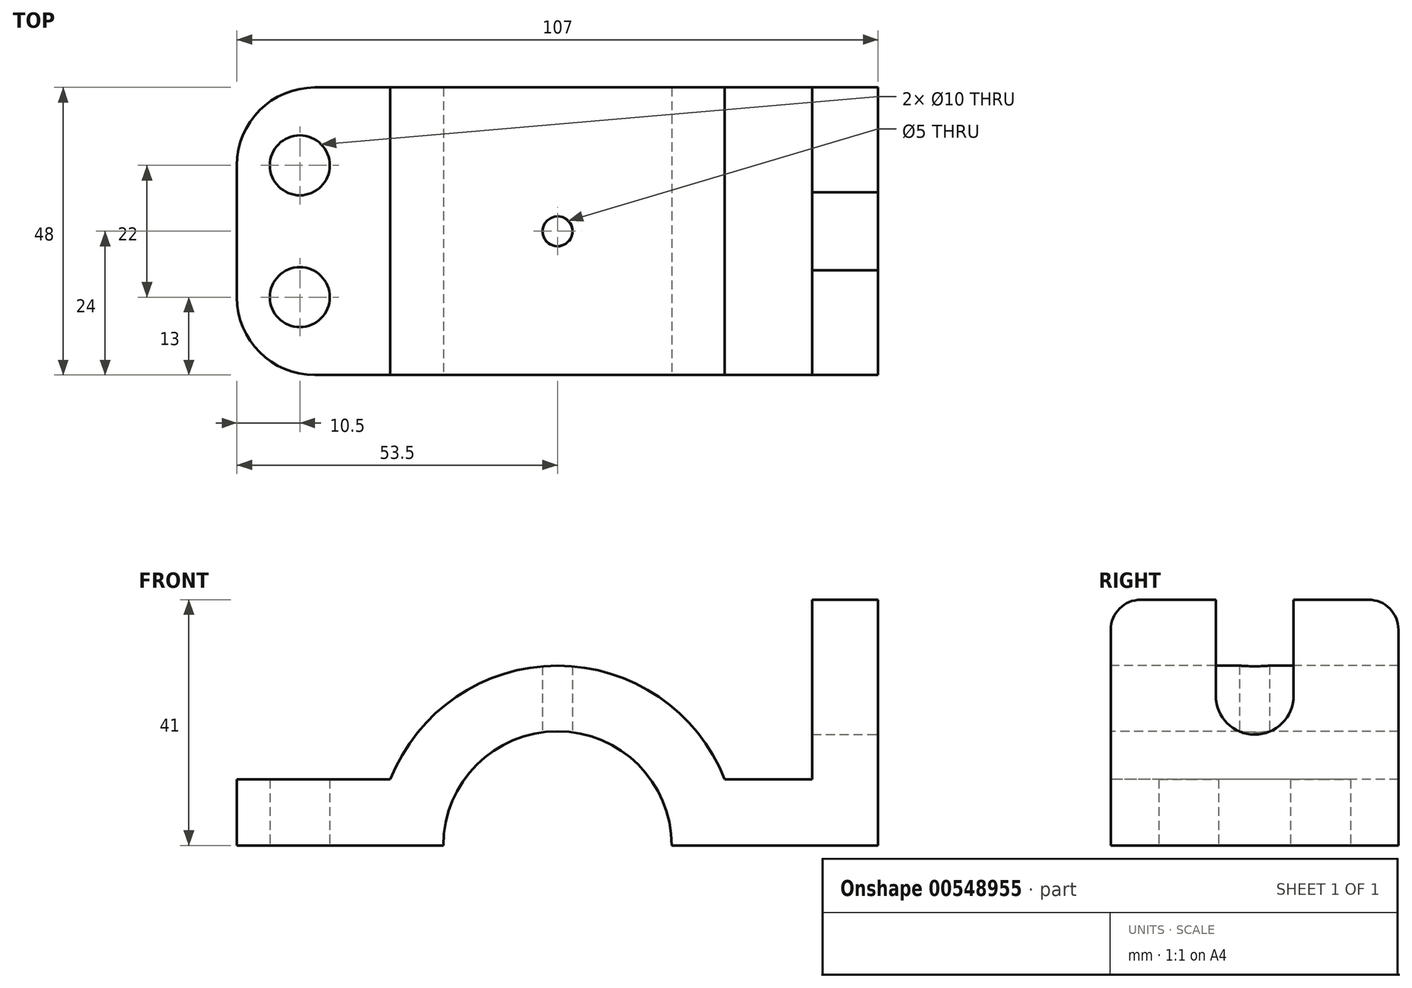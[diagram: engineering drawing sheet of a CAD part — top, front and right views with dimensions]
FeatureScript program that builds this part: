
annotation { "Feature Type Name" : "Feature", "Feature Type Description" : "" }
export const myFeature = defineFeature(function(context is Context, id is Id, definition is map)
    precondition{}
    {
        {
            var Q0;
            Q0=qCreatedBy(makeId("Front.planeOp"),FACE);
            var sketch = newSketch(context, id + "F0", { "sketchPlane" : qUnion([Q0])});
            skLineSegment(sketch, "E0.bottom", {"start": v(-53.5, 41) * mm, "end": v(53.5, 41) * mm});
            skLineSegment(sketch, "E0.left", {"start": v(-53.5, 41) * mm, "end": v(-53.5, 0) * mm});
            skLineSegment(sketch, "E0.right", {"start": v(53.5, 41) * mm, "end": v(53.5, 0) * mm});
            skPoint(sketch, "E0.middle", {"position": v(0, 0) * mm});
            skLineSegment(sketch, "E1", {"start": v(-53.5, 0) * mm, "end": v(53.5, 0) * mm});
            skPoint(sketch, "E0.top.start.orphan", {"position": v(-53.5, -41) * mm});
            skPoint(sketch, "E2.orphan", {"position": v(53.5, -41) * mm});
            skSolve(sketch);
        }
        {
            var Q0;
            Q0 = qSketchRegion(id + "F0", true);
            extrude(context, id + "F1", {"entities" : qUnion([Q0]), "endBound" : BoundingType.SYMMETRIC, "depth" : 48 * mm, "offsetDistance" : 25 * mm});
        }
        {
            var Q0;
            Q0=makeQuery(id+"F1.opExtrude","CAP_FACE",FACE,{"disambiguationData":[OSD([sQuery(id+"F0.wireOp",EDGE,"E0.bottom"),sQuery(id+"F0.wireOp",EDGE,"E0.left"),sQuery(id+"F0.wireOp",EDGE,"E0.right"),sQuery(id+"F0.wireOp",EDGE,"E1")])],"isStart":false});
            var sketch = newSketch(context, id + "F2", { "sketchPlane" : qUnion([Q0])});
            skArc(sketch, "E3", {"start": v(27.91, 11) * mm, "mid": v(0, 30) * mm, "end": v(-27.91, 11) * mm});
            skArc(sketch, "E4", {"start": v(19.05, 0) * mm, "mid": v(0, 19.05) * mm, "end": v(-19.05, 0) * mm});
            skLineSegment(sketch, "E5.0", {"start": v(-19.05, 0) * mm, "end": v(19.05, 0) * mm});
            skLineSegment(sketch, "E6", {"start": v(27.91, 11) * mm, "end": v(42.5, 11) * mm});
            skLineSegment(sketch, "E7", {"start": v(42.5, 11) * mm, "end": v(42.5, 41) * mm});
            skLineSegment(sketch, "E8", {"start": v(42.5, 41) * mm, "end": v(53.5, 41) * mm});
            skLineSegment(sketch, "E9", {"start": v(-27.91, 11) * mm, "end": v(-53.5, 11) * mm});
            skLineSegment(sketch, "E10", {"start": v(-53.5, 11) * mm, "end": v(-53.5, 41) * mm});
            skLineSegment(sketch, "E11", {"start": v(-53.5, 41) * mm, "end": v(42.5, 41) * mm});
            skPoint(sketch, "E12.orphan", {"position": v(-53.5, 0) * mm});
            skPoint(sketch, "E13.end.orphan", {"position": v(53.5, 0) * mm});
            skSolve(sketch);
        }
        {
            var Q0;
            Q0 = qSketchRegion(id + "F2", true);
            extrude(context, id + "F3", {"entities" : qUnion([Q0]), "operationType" : NewBodyOperationType.REMOVE, "endBound" : BoundingType.THROUGH_ALL, "oppositeDirection" : true, "depth" : 25 * mm, "offsetDistance" : 25 * mm});
        }
        {
            var Q0;
            Q0=makeQuery(id+"F1.opExtrude","CAP_EDGE",EDGE,{"disambiguationData":[OSD([sQuery(id+"F0.wireOp",EDGE,"E0.bottom")])],"isStart":false});
            var Q1;
            Q1=makeQuery(id+"F1.opExtrude","CAP_EDGE",EDGE,{"disambiguationData":[OSD([sQuery(id+"F0.wireOp",EDGE,"E0.bottom")])],"isStart":true});
            fillet(context, id + "F4", {"entities" : qUnion([Q0, Q1]), "radius" : 5 * mm, "tangentPropagation" : true, "allowEdgeOverflow" : false});
        }
        {
            var Q0;
            Q0=makeQuery(id+"F1.opExtrude","CAP_EDGE",EDGE,{"disambiguationData":[OSD([sQuery(id+"F0.wireOp",EDGE,"E0.left")])],"isStart":false});
            var Q1;
            Q1=makeQuery(id+"F1.opExtrude","CAP_EDGE",EDGE,{"disambiguationData":[OSD([sQuery(id+"F0.wireOp",EDGE,"E0.left")])],"isStart":true});
            fillet(context, id + "F5", {"entities" : qUnion([Q0, Q1]), "radius" : 13 * mm, "tangentPropagation" : true, "allowEdgeOverflow" : false});
        }
        {
            var Q0;
            Q0=qCreatedBy(makeId("Top.planeOp"),FACE);
            var sketch = newSketch(context, id + "F6", { "sketchPlane" : qUnion([Q0])});
            skCircle(sketch, "E14", {"center": v(0, 0) * mm, "radius": 2.5 * mm});
            skCircle(sketch, "E15", {"center": v(-43, -11) * mm, "radius": 5 * mm});
            skCircle(sketch, "E16", {"center": v(-43, 11) * mm, "radius": 5 * mm});
            skSolve(sketch);
        }
        {
            var Q0;
            Q0 = qSketchRegion(id + "F6", true);
            extrude(context, id + "F7", {"entities" : qUnion([Q0]), "operationType" : NewBodyOperationType.REMOVE, "endBound" : BoundingType.THROUGH_ALL, "depth" : 25 * mm, "offsetDistance" : 25 * mm});
        }
        {
            var Q0;
            Q0=makeQuery(id+"F1.opExtrude","SWEPT_FACE",FACE,{"disambiguationData":[OSD([sQuery(id+"F0.wireOp",EDGE,"E0.right")])]});
            var sketch = newSketch(context, id + "F8", { "sketchPlane" : qUnion([Q0])});
            skLineSegment(sketch, "E17.bottom", {"start": v(-6.5, 41) * mm, "end": v(6.5, 41) * mm});
            skLineSegment(sketch, "E17.left", {"start": v(-6.5, 41) * mm, "end": v(-6.5, 25) * mm});
            skLineSegment(sketch, "E17.right", {"start": v(6.5, 41) * mm, "end": v(6.5, 25) * mm});
            skArc(sketch, "E18", {"start": v(-6.5, 25) * mm, "mid": v(0, 18.5) * mm, "end": v(6.5, 25) * mm});
            skSolve(sketch);
        }
        {
            var Q0;
            Q0 = qSketchRegion(id + "F8", true);
            extrude(context, id + "F9", {"entities" : qUnion([Q0]), "operationType" : NewBodyOperationType.REMOVE, "endBound" : BoundingType.UP_TO_NEXT, "oppositeDirection" : true, "depth" : 25 * mm, "offsetDistance" : 25 * mm});
        }
    });
